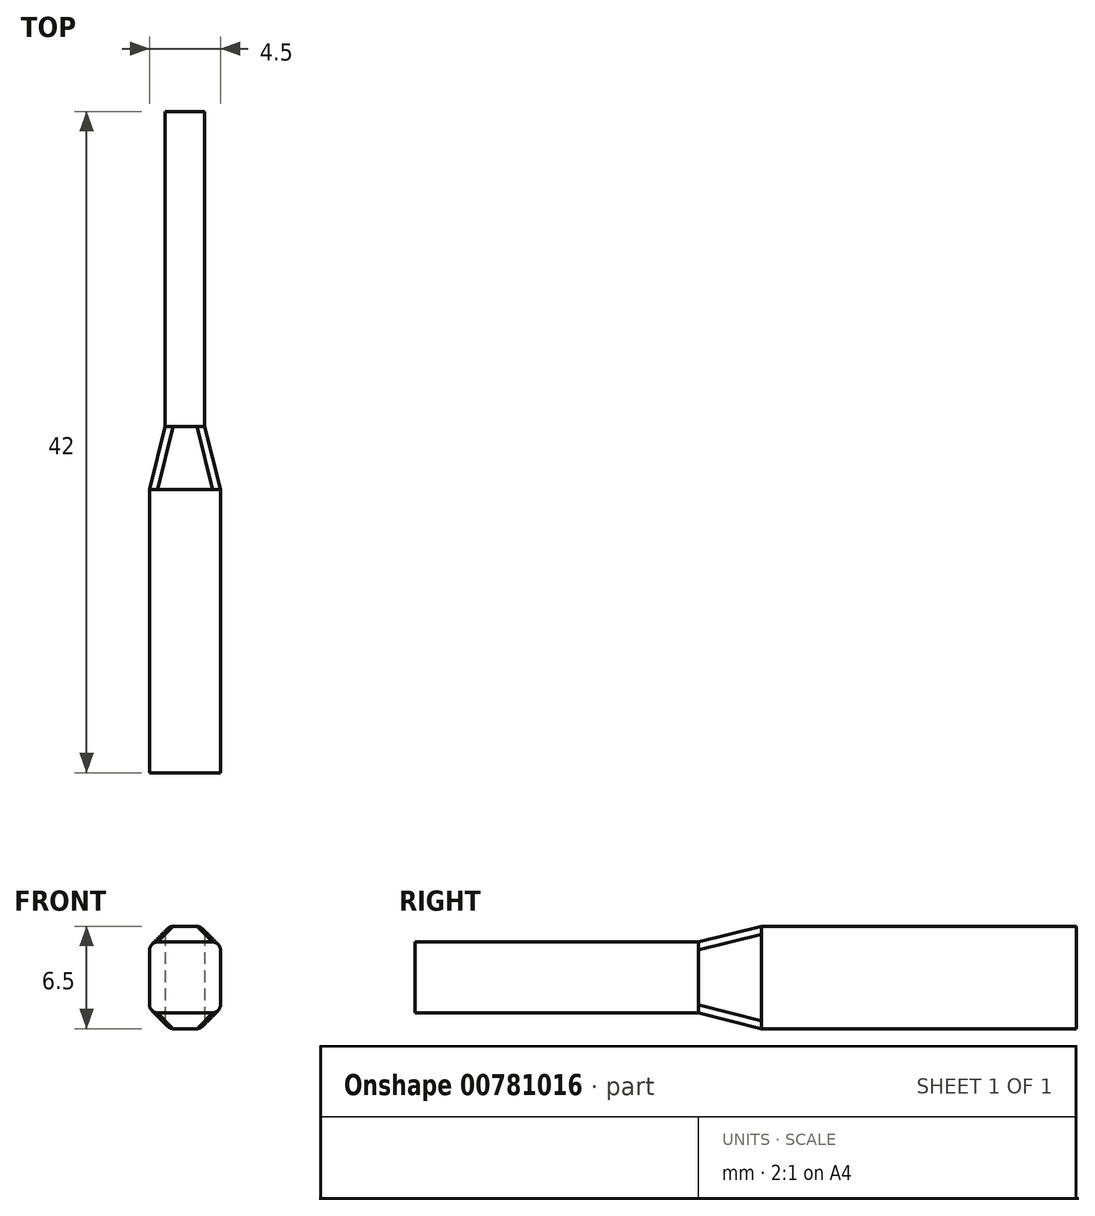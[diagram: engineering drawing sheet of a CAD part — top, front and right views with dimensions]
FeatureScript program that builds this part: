
annotation { "Feature Type Name" : "Feature", "Feature Type Description" : "" }
export const myFeature = defineFeature(function(context is Context, id is Id, definition is map)
    precondition{}
    {
        {
            var Q0;
            Q0=qCreatedBy(makeId("Front.planeOp"),FACE);
            var sketch = newSketch(context, id + "F0", { "sketchPlane" : qUnion([Q0])});
            skLineSegment(sketch, "E0.bottom", {"start": v(-2.25, -2.25) * mm, "end": v(2.25, -2.25) * mm});
            skLineSegment(sketch, "E0.top", {"start": v(-2.25, 2.25) * mm, "end": v(2.25, 2.25) * mm});
            skLineSegment(sketch, "E0.left", {"start": v(-2.25, -2.25) * mm, "end": v(-2.25, 2.25) * mm});
            skLineSegment(sketch, "E0.right", {"start": v(2.25, -2.25) * mm, "end": v(2.25, 2.25) * mm});
            skLineSegment(sketch, "E1.bottom", {"start": v(-1.25, 3.25) * mm, "end": v(1.25, 3.25) * mm});
            skLineSegment(sketch, "E1.top", {"start": v(-1.25, -3.25) * mm, "end": v(1.25, -3.25) * mm});
            skLineSegment(sketch, "E1.left", {"start": v(-1.25, 3.25) * mm, "end": v(-1.25, -3.25) * mm});
            skLineSegment(sketch, "E1.right", {"start": v(1.25, 3.25) * mm, "end": v(1.25, -3.25) * mm});
            skSolve(sketch);
        }
        {
            var Q0;
            {var subQ0=sQuery(id+"F0.wireOp",EDGE,"E1.left");var subQ1=sQuery(id+"F0.wireOp",EDGE,"E0.bottom");var subQ2=makeQuery(id+"F0.imprint","INTERSECT",VERTEX,{"derivedFrom":[subQ1,subQ0]});Q0=makeQuery(id+"F0.imprint","IMPRINT",FACE,{"disambiguationData":[TD([[makeQuery(id+"F0.imprint","IMPRINT",EDGE,{"disambiguationData":[TD([[subQ2,-1.0]])],"derivedFrom":subQ1}),1.0]])]});}
            var Q1;
            {var subQ0=sQuery(id+"F0.wireOp",EDGE,"E0.right");Q1=makeQuery(id+"F0.imprint","IMPRINT",FACE,{"disambiguationData":[TD([[makeQuery(id+"F0.imprint","IMPRINT",EDGE,{"derivedFrom":subQ0}),1.0]])]});}
            var Q2;
            {var subQ0=sQuery(id+"F0.wireOp",EDGE,"E0.left");Q2=makeQuery(id+"F0.imprint","IMPRINT",FACE,{"disambiguationData":[TD([[makeQuery(id+"F0.imprint","IMPRINT",EDGE,{"derivedFrom":subQ0}),-1.0]])]});}
            extrude(context, id + "F1", {"entities" : qUnion([Q0, Q1, Q2]), "depth" : 20 * mm, "offsetDistance" : 25 * mm});
        }
        {
            var Q0;
            {var subQ5=sQuery(id+"F0.wireOp",EDGE,"E1.bottom");Q0=makeQuery(id+"F0.imprint","IMPRINT",FACE,{"disambiguationData":[TD([[makeQuery(id+"F0.imprint","IMPRINT",EDGE,{"derivedFrom":subQ5}),-1.0]])]});}
            var Q1;
            {var subQ0=sQuery(id+"F0.wireOp",EDGE,"E1.left");var subQ1=sQuery(id+"F0.wireOp",EDGE,"E0.bottom");var subQ2=makeQuery(id+"F0.imprint","INTERSECT",VERTEX,{"derivedFrom":[subQ1,subQ0]});Q1=makeQuery(id+"F0.imprint","IMPRINT",FACE,{"disambiguationData":[TD([[makeQuery(id+"F0.imprint","IMPRINT",EDGE,{"disambiguationData":[TD([[subQ2,-1.0]])],"derivedFrom":subQ1}),1.0]])]});}
            var Q2;
            {var subQ5=sQuery(id+"F0.wireOp",EDGE,"E1.top");Q2=makeQuery(id+"F0.imprint","IMPRINT",FACE,{"disambiguationData":[TD([[makeQuery(id+"F0.imprint","IMPRINT",EDGE,{"derivedFrom":subQ5}),1.0]])]});}
            extrude(context, id + "F2", {"entities" : qUnion([Q0, Q1, Q2]), "operationType" : NewBodyOperationType.ADD, "oppositeDirection" : true, "depth" : 22 * mm, "offsetDistance" : 25 * mm});
        }
        {
            var Q0;
            Q0=makeQuery(id+"F1.opExtrude","SWEPT_EDGE",EDGE,{"disambiguationData":[OSD([sQuery(id+"F0.wireOp",EDGE,"E0.top"),sQuery(id+"F0.wireOp",EDGE,"E0.left")])]});
            var Q1;
            Q1=makeQuery(id+"F2.opExtrude","SWEPT_EDGE",EDGE,{"disambiguationData":[OSD([sQuery(id+"F0.wireOp",EDGE,"E1.bottom"),sQuery(id+"F0.wireOp",EDGE,"E1.left")])]});
            var Q2;
            Q2=makeQuery(id+"F2.opExtrude","SWEPT_EDGE",EDGE,{"disambiguationData":[OSD([sQuery(id+"F0.wireOp",EDGE,"E1.bottom"),sQuery(id+"F0.wireOp",EDGE,"E1.right")])]});
            var Q3;
            Q3=makeQuery(id+"F2.opExtrude","SWEPT_EDGE",EDGE,{"disambiguationData":[OSD([sQuery(id+"F0.wireOp",EDGE,"E1.top"),sQuery(id+"F0.wireOp",EDGE,"E1.left")])]});
            var Q4;
            Q4=makeQuery(id+"F1.opExtrude","SWEPT_EDGE",EDGE,{"disambiguationData":[OSD([sQuery(id+"F0.wireOp",EDGE,"E0.bottom"),sQuery(id+"F0.wireOp",EDGE,"E0.left")])]});
            var Q5;
            Q5=makeQuery(id+"F2.opExtrude","SWEPT_EDGE",EDGE,{"disambiguationData":[OSD([sQuery(id+"F0.wireOp",EDGE,"E1.top"),sQuery(id+"F0.wireOp",EDGE,"E1.right")])]});
            var Q6;
            Q6=makeQuery(id+"F1.opExtrude","SWEPT_EDGE",EDGE,{"disambiguationData":[OSD([sQuery(id+"F0.wireOp",EDGE,"E0.bottom"),sQuery(id+"F0.wireOp",EDGE,"E0.right")])]});
            var Q7;
            Q7=makeQuery(id+"F1.opExtrude","SWEPT_EDGE",EDGE,{"disambiguationData":[OSD([sQuery(id+"F0.wireOp",EDGE,"E0.top"),sQuery(id+"F0.wireOp",EDGE,"E0.right")])]});
            fillet(context, id + "F3", {"entities" : qUnion([Q0, Q1, Q2, Q3, Q4, Q5, Q6, Q7]), "radius" : 0.5 * mm, "tangentPropagation" : true, "allowEdgeOverflow" : false});
        }
        {
            var Q0;
            Q0=qCreatedBy(makeId("Right.planeOp"),FACE);
            var sketch = newSketch(context, id + "F4", { "sketchPlane" : qUnion([Q0])});
            skLineSegment(sketch, "E2.bottom", {"start": v(-2, 5) * mm, "end": v(2, 5) * mm});
            skLineSegment(sketch, "E2.top", {"start": v(-2, -5) * mm, "end": v(2, -5) * mm});
            skLineSegment(sketch, "E2.left", {"start": v(-2, 5) * mm, "end": v(-2, -5) * mm});
            skLineSegment(sketch, "E2.right", {"start": v(2, 5) * mm, "end": v(2, -5) * mm});
            skSolve(sketch);
        }
        {
            var Q0;
            Q0 = qSketchRegion(id + "F4", true);
            extrude(context, id + "F5", {"entities" : qUnion([Q0]), "operationType" : NewBodyOperationType.REMOVE, "endBound" : BoundingType.SYMMETRIC, "depth" : 25 * mm, "offsetDistance" : 25 * mm});
        }
        {
            var Q0;
            Q0=makeQuery(id+"F5.boolean.opBoolean","COPY",FACE,{"derivedFrom":makeQuery(id+"F5.opExtrude","SWEPT_FACE",FACE,{"disambiguationData":[OSD([sQuery(id+"F4.wireOp",EDGE,"E2.right")])]})});
            var Q1;
            Q1=makeQuery(id+"F5.boolean.opBoolean","COPY",FACE,{"derivedFrom":makeQuery(id+"F5.opExtrude","SWEPT_FACE",FACE,{"disambiguationData":[OSD([sQuery(id+"F4.wireOp",EDGE,"E2.left")])]})});
            loft(context, id + "F6", {"sheetProfilesArray" : [{ "sheetProfileEntities" : qUnion([Q0]) }, { "sheetProfileEntities" : qUnion([Q1]) }]});
        }
    });
